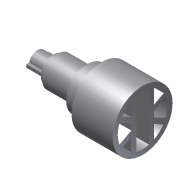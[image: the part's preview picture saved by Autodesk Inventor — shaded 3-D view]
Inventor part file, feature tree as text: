
AUTODESK INVENTOR PART (.ipt)
format: ipt  version: 2012 (Build 160160000, 160)  size: 229,376 bytes
history: native  units: mm
features: sketch x7, extrude x6, revolve x1
ambient origin geometry x8: Origin, YZ Plane, XZ Plane, XY Plane, X Axis, Y Axis, Z Axis, Center Point
bodies: Solid1 (feature_tree)
feature tree (14):
  revolve  "Revolution1"  [1 undecoded]
  extrude  "Extrusion1"  Depth=3.45mm
  extrude  "Extrusion2"  Depth=2.4mm
  extrude  "Extrusion3"  Depth=1.05mm
  extrude  "Extrusion4"  Depth=1.7mm
  extrude  "Extrusion5"  Depth=2.5mm
  extrude  "Extrusion6"  Depth=23.8mm
  sketch  "Sketch1"  dims[d0=11.9mm d1=6.2mm]
  sketch  "Sketch2"  dims[d2=10.2mm d3=3.45mm]
  sketch  "Sketch3"  dims[d4=5.6mm d5=2.4mm]
  sketch  "Sketch4"  dims[d6=11.9mm d7=1.05mm]
  sketch  "Sketch5"  dims[d8=1.6mm d9=1.7mm]
  sketch  "Sketch7"  dims[d11=90.0deg d12=2.5mm]
  sketch  "Sketch8"  dims[d13=10.0mm d14=0.0mm d15=23.8mm d16=19.8mm d17=2.0mm d18=2.5mm d19=2.0mm d20=2.0mm d24=2.0mm d25=2.0mm d26=2.0mm d27=2.0mm d28=2.5mm d29=12.0mm d30=0.0mm d32=0.0mm d33=0.0mm d36=7.0mm d37=0.0mm d38=23.0mm d39=0.0mm d40=4.4mm d42=1.2mm d44=1.2mm d46=16.0mm d47=14.0mm d48=0.0mm d49=7.5mm d50=7.5mm d51=14.0mm d52=20.0mm d53=0.0mm d54=6.4mm]
note: 1 required parameter value undecoded (feature->parameter linkage not recoverable at this tier; creation-order binding heuristic only, values carry confidence <= 0.55)
